# Revit family: 113941001_Lavamanos Toscano
name_source: partatom
category: Plumbing Fixtures
units: mm (PartAtom-declared; Revit-internal decimal feet)

## family parameters
Cut with Voids When Loaded = No
Host = Face
OmniClass Number = 23.31.13.11
OmniClass Title = Single Sinks
Part Type = Normal
Room Calculation Point = No
Round Connector Dimension = Use Diameter
Shared = No

## types (1)
- 113941001_Lavamanos Toscano
    Alto = 107 mm  [stored 0.35105 ft]
    Ancho = 342 mm  [stored 1.12205 ft]
    Colección = Minimal ll
    Creado por = BIMBAU
    Default Elevation = 1219 mm
    Description = Está elaborado en porcelana sanitaria y cuenta con el tamaño 34.2 x 34. 2 x 10.7 cm.
    Fecha de creación = 07/04/2021
    Forma = Redondo
    Garantía = Garantía Integral de por vida.
    Manufacturer = Corona
    Material = Corona_Porcelana_Sanitaria
    Material 2 = Corona_Acero inoxidable
    Model = Toscano
    Normatividad = ASME/ANSI A112.19.2Garantía.
    Peso = 11 lbs. (5.2 kg).
    Pozo = 34.2 cms x 34.2 cms x 10.7 cms.
    Profundidad = 342 mm  [stored 1.12205 ft]
    Profundidad del Pozo = 10.7 cm
    Referencia = 113941001
    URL = https://corona.co
    Uso = Residencial

note: [stored X ft] marks values corroborated as IEEE doubles in the binary element streams (Revit-internal decimal feet)

## geometry (parser evidence)
native form markers: Sweep x7
no freeform markers — native parametric forms only
